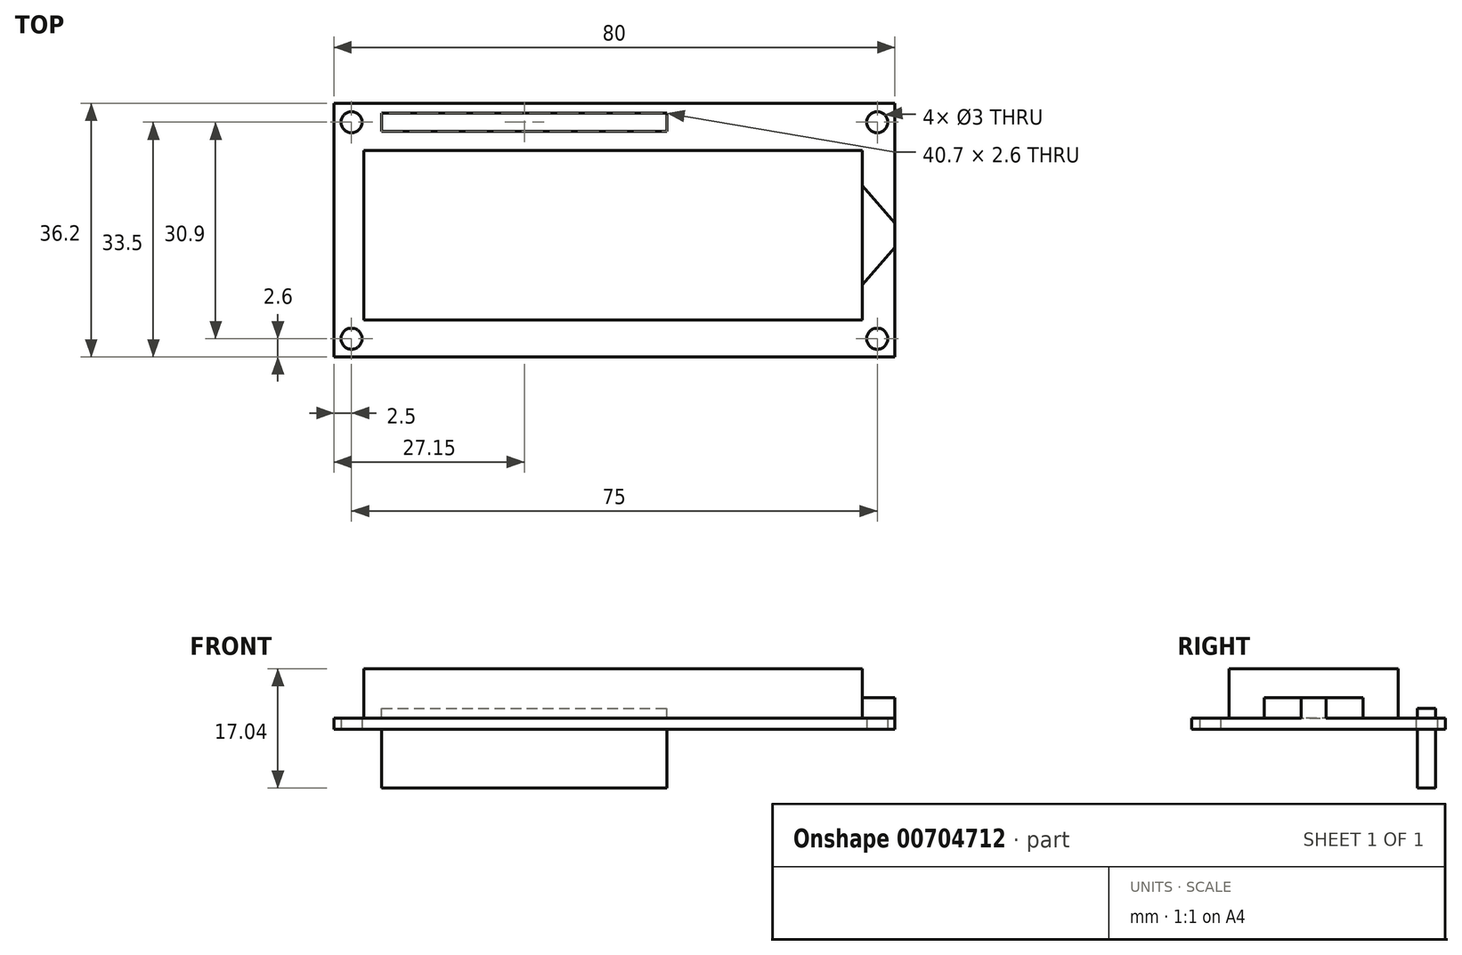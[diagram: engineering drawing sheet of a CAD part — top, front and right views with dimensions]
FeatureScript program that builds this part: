
annotation { "Feature Type Name" : "Feature", "Feature Type Description" : "" }
export const myFeature = defineFeature(function(context is Context, id is Id, definition is map)
    precondition{}
    {
        {
            var Q0;
            Q0=qCreatedBy(makeId("Top.planeOp"),FACE);
            var sketch = newSketch(context, id + "F0", { "sketchPlane" : qUnion([Q0])});
            skLineSegment(sketch, "E0.bottom", {"start": v(-40, 18.1) * mm, "end": v(40, 18.1) * mm});
            skLineSegment(sketch, "E0.top", {"start": v(-40, -18.1) * mm, "end": v(40, -18.1) * mm});
            skLineSegment(sketch, "E0.left", {"start": v(-40, 18.1) * mm, "end": v(-40, -18.1) * mm});
            skLineSegment(sketch, "E0.right", {"start": v(40, 18.1) * mm, "end": v(40, -18.1) * mm});
            skLineSegment(sketch, "E1.bottom", {"start": v(-35.75, 11.35) * mm, "end": v(35.35, 11.35) * mm});
            skLineSegment(sketch, "E1.top", {"start": v(-35.75, -12.8) * mm, "end": v(35.35, -12.8) * mm});
            skLineSegment(sketch, "E1.left", {"start": v(-35.75, 11.35) * mm, "end": v(-35.75, -12.8) * mm});
            skLineSegment(sketch, "E1.right", {"start": v(35.35, 11.35) * mm, "end": v(35.35, -12.8) * mm});
            skCircle(sketch, "E2", {"center": v(37.5, 15.4) * mm, "radius": 1.5 * mm});
            skCircle(sketch, "E3", {"center": v(37.5, -15.5) * mm, "radius": 1.5 * mm});
            skCircle(sketch, "E4", {"center": v(-37.5, -15.5) * mm, "radius": 1.5 * mm});
            skCircle(sketch, "E5", {"center": v(-37.5, 15.4) * mm, "radius": 1.5 * mm});
            skLineSegment(sketch, "E6.bottom", {"start": v(-33.2, 16.7) * mm, "end": v(7.5, 16.7) * mm});
            skLineSegment(sketch, "E6.top", {"start": v(-33.2, 14.1) * mm, "end": v(7.5, 14.1) * mm});
            skLineSegment(sketch, "E6.left", {"start": v(-33.2, 16.7) * mm, "end": v(-33.2, 14.1) * mm});
            skLineSegment(sketch, "E6.right", {"start": v(7.5, 16.7) * mm, "end": v(7.5, 14.1) * mm});
            skLineSegment(sketch, "E7", {"start": v(35.35, 6.35) * mm, "end": v(40, 1.03) * mm});
            skLineSegment(sketch, "E8", {"start": v(40, -2.47) * mm, "end": v(35.35, -7.8) * mm});
            skSolve(sketch);
        }
        {
            var Q0;
            Q0=makeQuery(id+"F0.imprint","IMPRINT",FACE,{"disambiguationData":[TD([[makeQuery(id+"F0.imprint","IMPRINT",EDGE,{"derivedFrom":sQuery(id+"F0.wireOp",EDGE,"E0.bottom")}),-1.0]])]});
            var Q1;
            Q1=makeQuery(id+"F0.imprint","IMPRINT",FACE,{"disambiguationData":[TD([[makeQuery(id+"F0.imprint","IMPRINT",EDGE,{"derivedFrom":sQuery(id+"F0.wireOp",EDGE,"E1.bottom")}),-1.0]])]});
            extrude(context, id + "F1", {"entities" : qUnion([Q0, Q1]), "depth" : 1.6 * mm, "offsetDistance" : 25 * mm});
        }
        {
            var Q0;
            Q0=makeQuery(id+"F0.imprint","IMPRINT",FACE,{"disambiguationData":[TD([[makeQuery(id+"F0.imprint","IMPRINT",EDGE,{"derivedFrom":sQuery(id+"F0.wireOp",EDGE,"E1.bottom")}),-1.0]])]});
            extrude(context, id + "F2", {"entities" : qUnion([Q0]), "operationType" : NewBodyOperationType.ADD, "depth" : 8.64 * mm, "offsetDistance" : 25 * mm});
        }
        {
            var Q0;
            Q0=makeQuery(id+"F0.imprint","IMPRINT",FACE,{"disambiguationData":[TD([[makeQuery(id+"F0.imprint","IMPRINT",EDGE,{"derivedFrom":sQuery(id+"F0.wireOp",EDGE,"E6.bottom")}),-1.0]])]});
            extrude(context, id + "F3", {"entities" : qUnion([Q0]), "operationType" : NewBodyOperationType.ADD, "oppositeDirection" : true, "depth" : 8.4 * mm, "offsetDistance" : 25 * mm, "hasSecondDirection" : true, "secondDirectionOppositeDirection" : false, "secondDirectionDepth" : 3 * mm});
        }
        {
            var Q0;
            {var subQ0=sQuery(id+"F0.wireOp",EDGE,"E7");Q0=makeQuery(id+"F0.imprint","IMPRINT",FACE,{"disambiguationData":[TD([[makeQuery(id+"F0.imprint","IMPRINT",EDGE,{"derivedFrom":subQ0}),-1.0]])]});}
            extrude(context, id + "F4", {"entities" : qUnion([Q0]), "operationType" : NewBodyOperationType.ADD, "depth" : 4.5 * mm, "offsetDistance" : 25 * mm});
        }
    });
